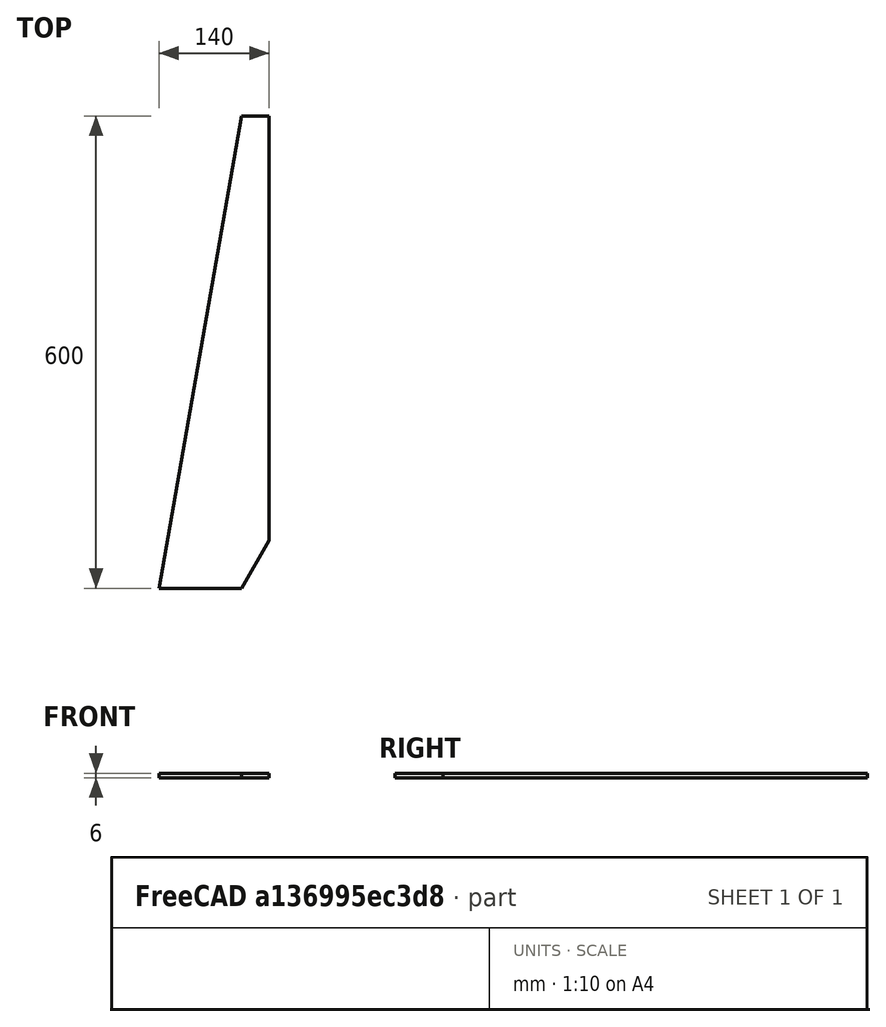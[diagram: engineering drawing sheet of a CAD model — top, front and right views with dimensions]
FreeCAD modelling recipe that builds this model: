
FCSTD DOCUMENT  (FreeCAD 0.21R33771 (Git))
Label: Blade_Template
License: All rights reserved
LicenseURL: https://en.wikipedia.org/wiki/All_rights_reserved
objects: Spreadsheet::Sheet×1, Sketcher::SketchObject×1, PartDesign::Pad×1, PartDesign::Body×1
note: 4 computed .brp shape members not serialized (recipe doc carries the construction recipe); baked Part::Feature solids carry a one-line shape summary decoded from their .brp
EXTERNAL_REF file=../Master_of_Puppets.FCStd obj=Blade

FEATURE [Spreadsheet::Sheet] Spreadsheet
  cells = A1='Inputs; A2='BladeRadius; B2(BladeRadius)==Master_of_Puppets#Blade.BladeRadius; A3='BladeTemplateDim_V; B3(BladeTemplateDim_V)==Master_of_Puppets#Blade.BladeTemplateDim_V; A4='BladeTemplateDim_W; B4(BladeTemplateDim_W)==Master_of_Puppets#Blade.BladeTemplateDim_W; A5='BladeTemplateThickness; B5(BladeTemplateThickness)==Master_of_Puppets#Blade.BladeTemplateThickness
FEATURE [Sketcher::SketchObject] Sketch
  FullyConstrained = true
  MapMode = 5
  Support = -> [XY_Plane]
  expr: Constraints[12] = Spreadsheet.BladeTemplateDim_V
  expr: Constraints[5] = Spreadsheet.BladeTemplateDim_W
  expr: Constraints[6] = Spreadsheet.BladeRadius
  expr: Constraints[7] = Spreadsheet.BladeTemplateDim_W
  sketch-geometry (5):
    g0: LineSegment StartX=0 StartY=0 StartZ=0 EndX=35 EndY=60.6218 EndZ=0
    g1: LineSegment StartX=35 StartY=60.6218 StartZ=0 EndX=35 EndY=600 EndZ=0
    g2: LineSegment StartX=35 StartY=600 StartZ=0 EndX=0 EndY=600 EndZ=0
    g3: LineSegment StartX=0 StartY=600 StartZ=0 EndX=-105 EndY=0 EndZ=0
    g4: LineSegment StartX=-105 StartY=0 StartZ=0 EndX=0 EndY=0 EndZ=0
  constraints (14):
    c: Coincident(g0,g1)
    c: Vertical(g1)
    c: Coincident(g1,g2)
    c: Horizontal(g2)
    c: Coincident(g2,g3)
    c: DistanceX(g2,g1) = 35
    c: DistanceY(g0,g1) = 600
    c: DistanceX(g0,g0) = 35
    c: Coincident(g4,g3)
    c: Coincident(g4,g0)
    c: Horizontal(g4)
    c: Coincident(g0,g-1)
    c: DistanceX(g3,g0) = 140
    c: Angle(g0,g4) = 2.0944
FEATURE [PartDesign::Pad] Pad
  Direction = (0,0,1)
  Length = 6
  Length2 = 10
  Profile = -> Sketch
  ReferenceAxis = -> Sketch [N_Axis]
  Type = 0
  expr: Length = Spreadsheet.BladeTemplateThickness
FEATURE [PartDesign::Body] Body  label="Blade_Template"
  Group = -> [Sketch,Pad]
  Openafpm_Flat = true
  Origin = -> Origin
  Tip = -> Pad
